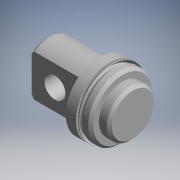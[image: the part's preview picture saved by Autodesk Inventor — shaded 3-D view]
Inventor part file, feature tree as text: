
AUTODESK INVENTOR PART (.ipt)
format: ipt  version: 2017.3 (Build 213256000, 256)  size: 229,888 bytes
history: native  units: mm (DEFAULTED — no unit token found)
features: other x140, sketch x6, revolve x4, extrude x2
ambient origin geometry x8: Origin, YZ Plane, XZ Plane, XY Plane, X Axis, Y Axis, Z Axis, Center Point
bodies: Solid1 (feature_tree)
feature tree (152):
  revolve  "Revolution1"  Angle=360.0deg
  revolve  "Revolution2"  Angle=360.0deg
  revolve  "Revolution3"  [1 undecoded]
  revolve  "Revolution4"  [1 undecoded]
  extrude  "Extrusion1"  [1 undecoded]
  extrude  "Extrusion2"  [1 undecoded]
  other  "1_XY"
  other  "1_YZ"
  other  "1_ZX"
  other  "1_X"
  other  "1_Y"
  other  "1_Z"
  other  "1_Center"
  other  "lovra_XY"
  other  "lovra_YZ"
  other  "lovra_ZX"
  other  "lovra_X"
  other  "lovra_Y"
  other  "lovra_Z"
  other  "lovra_Center"
  other  "lovra1_XY"
  other  "lovra1_YZ"
  other  "lovra1_ZX"
  other  "lovra1_X"
  other  "lovra1_Y"
  other  "lovra1_Z"
  other  "lovra1_Center"
  other  "lovra2_XY"
  other  "lovra2_YZ"
  other  "lovra2_ZX"
  other  "lovra2_X"
  other  "lovra2_Y"
  other  "lovra2_Z"
  other  "lovra2_Center"
  other  "lovra21_XY"
  other  "lovra21_YZ"
  other  "lovra21_ZX"
  other  "lovra21_X"
  other  "lovra21_Y"
  other  "lovra21_Z"
  other  "lovra21_Center"
  other  "lovra22_XY"
  other  "lovra22_YZ"
  other  "lovra22_ZX"
  other  "lovra22_X"
  other  "lovra22_Y"
  other  "lovra22_Z"
  other  "lovra22_Center"
  other  "lovra3_XY"
  other  "lovra3_YZ"
  other  "lovra3_ZX"
  other  "lovra3_X"
  other  "lovra3_Y"
  other  "lovra3_Z"
  other  "lovra3_Center"
  other  "olen_XY"
  other  "olen_YZ"
  other  "olen_ZX"
  other  "olen_X"
  other  "olen_Y"
  other  "olen_Z"
  other  "olen_Center"
  other  "p1_XY"
  other  "p1_YZ"
  other  "p1_ZX"
  other  "p1_X"
  other  "p1_Y"
  other  "p1_Z"
  other  "p1_Center"
  other  "p2_XY"
  other  "p2_YZ"
  other  "p2_ZX"
  other  "p2_X"
  other  "p2_Y"
  other  "p2_Z"
  other  "p2_Center"
  other  "port2_XY"
  other  "port2_YZ"
  other  "port2_ZX"
  other  "port2_X"
  other  "port2_Y"
  other  "port2_Z"
  other  "port2_Center"
  other  "thd1_XY"
  other  "thd1_YZ"
  other  "thd1_ZX"
  other  "thd1_X"
  other  "thd1_Y"
  other  "thd1_Z"
  other  "thd1_Center"
  other  "thd2_XY"
  other  "thd2_YZ"
  other  "thd2_ZX"
  other  "thd2_X"
  other  "thd2_Y"
  other  "thd2_Z"
  other  "thd2_Center"
  other  "to_mounting_bracket_XY"
  other  "to_mounting_bracket_YZ"
  other  "to_mounting_bracket_ZX"
  other  "to_mounting_bracket_X"
  other  "to_mounting_bracket_Y"
  other  "to_mounting_bracket_Z"
  other  "to_mounting_bracket_Center"
  other  "to_nut_XY"
  other  "to_nut_YZ"
  other  "to_nut_ZX"
  other  "to_nut_X"
  other  "to_nut_Y"
  other  "to_nut_Z"
  other  "to_nut_Center"
  other  "to_pin_XY"
  other  "to_pin_YZ"
  other  "to_pin_ZX"
  other  "to_pin_X"
  other  "to_pin_Y"
  other  "to_pin_Z"
  other  "to_pin_Center"
  other  "to_pin_1_XY"
  other  "to_pin_1_YZ"
  other  "to_pin_1_ZX"
  other  "to_pin_1_X"
  other  "to_pin_1_Y"
  other  "to_pin_1_Z"
  other  "to_pin_1_Center"
  other  "to_pin_r_XY"
  other  "to_pin_r_YZ"
  other  "to_pin_r_ZX"
  other  "to_pin_r_X"
  other  "to_pin_r_Y"
  other  "to_pin_r_Z"
  other  "to_pin_r_Center"
  other  "to_screw_XY"
  other  "to_screw_YZ"
  other  "to_screw_ZX"
  other  "to_screw_X"
  other  "to_screw_Y"
  other  "to_screw_Z"
  other  "to_screw_Center"
  other  "to_tube_XY"
  other  "to_tube_YZ"
  other  "to_tube_ZX"
  other  "to_tube_X"
  other  "to_tube_Y"
  other  "to_tube_Z"
  other  "to_tube_Center"
  sketch  "Sketch_1"  dims[d0=360.0deg d1=360.0deg]
  sketch  "Sketch_24"  dims[d2=360.0deg d3=360.0deg]
  sketch  "Sketch_26"  dims[d4=15.875mm d5=0.0mm d6=18.923mm d7=0.0mm]
  sketch  "Sketch_27"  dims[d8=0.0mm d9=0.0mm d10=0.0mm d11=0.0mm d12=0.0mm d13=0.0mm d14=0.0mm]
  sketch  "Sketch_28"
  sketch  "Sketch_29"
note: 4 required parameter values undecoded (feature->parameter linkage not recoverable at this tier; creation-order binding heuristic only, values carry confidence <= 0.55)